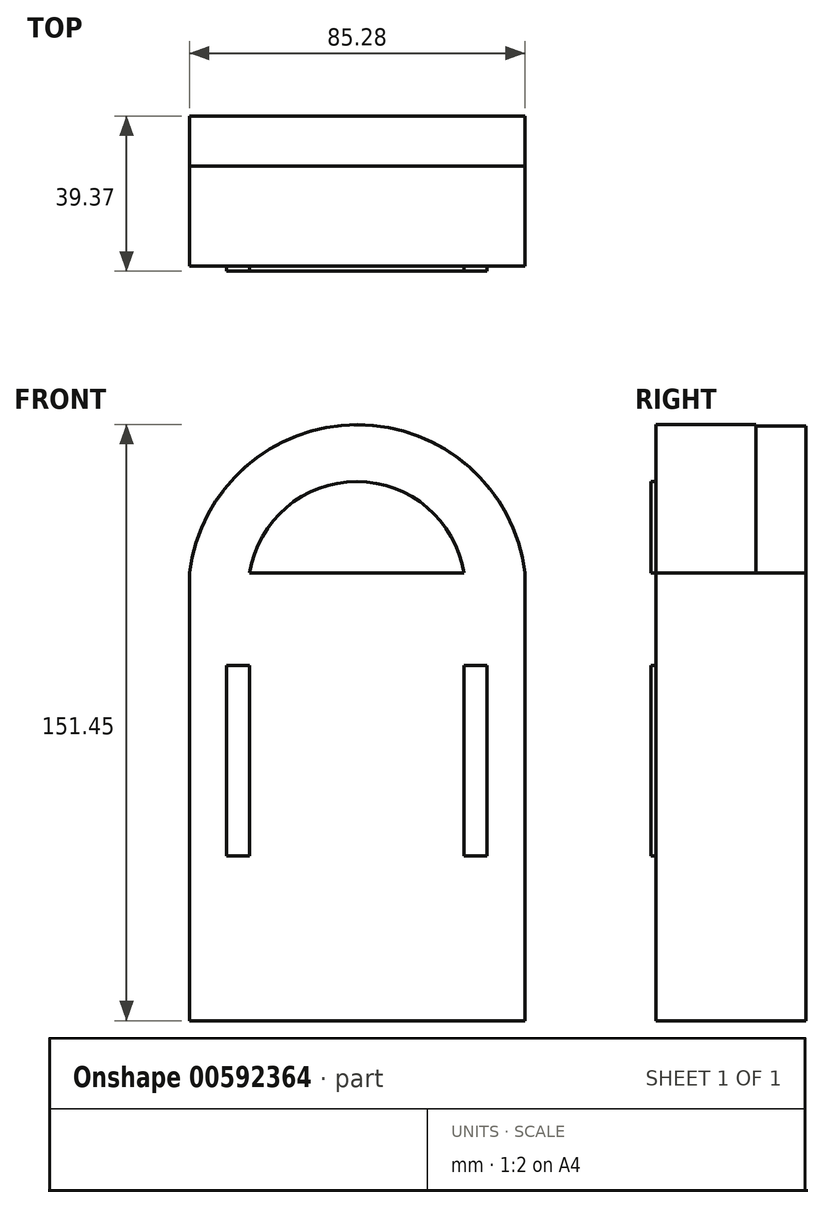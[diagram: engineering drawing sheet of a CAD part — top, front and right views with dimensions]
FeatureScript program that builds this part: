
annotation { "Feature Type Name" : "Feature", "Feature Type Description" : "" }
export const myFeature = defineFeature(function(context is Context, id is Id, definition is map)
    precondition{}
    {
        {
            var Q0;
            Q0=qCreatedBy(makeId("Front.planeOp"),FACE);
            var sketch = newSketch(context, id + "F0", { "sketchPlane" : qUnion([Q0])});
            skLineSegment(sketch, "E0", {"start": v(-42.64, 0) * mm, "end": v(0, 0) * mm});
            skLineSegment(sketch, "E1", {"start": v(0, 0) * mm, "end": v(42.64, 0) * mm});
            skLineSegment(sketch, "E2", {"start": v(-42.64, 0) * mm, "end": v(-42.64, 37.98) * mm});
            skLineSegment(sketch, "E3", {"start": v(42.64, 37.98) * mm, "end": v(42.64, 0) * mm});
            skLineSegment(sketch, "E4", {"start": v(-42.64, 0) * mm, "end": v(-42.64, -75.73) * mm});
            skLineSegment(sketch, "E5", {"start": v(-42.64, -75.73) * mm, "end": v(42.64, -75.73) * mm});
            skLineSegment(sketch, "E6", {"start": v(42.64, -75.73) * mm, "end": v(42.64, 0) * mm});
            skArc(sketch, "E7", {"start": v(42.64, 37.98) * mm, "mid": v(0, 75.72) * mm, "end": v(-42.64, 37.98) * mm});
            skSolve(sketch);
        }
        {
            var Q0;
            Q0=makeQuery(id+"F0.imprint","IMPRINT",FACE,{"disambiguationData":[TD([[makeQuery(id+"F0.imprint","IMPRINT",EDGE,{"derivedFrom":sQuery(id+"F0.wireOp",EDGE,"E0")}),1.0]])]});
            var Q1;
            Q1=makeQuery(id+"F0.imprint","IMPRINT",FACE,{"disambiguationData":[TD([[makeQuery(id+"F0.imprint","IMPRINT",EDGE,{"derivedFrom":sQuery(id+"F0.wireOp",EDGE,"E0")}),-1.0]])]});
            extrude(context, id + "F1", {"entities" : qUnion([Q0, Q1]), "depth" : 25.4 * mm, "offsetDistance" : 25.4 * mm});
        }
        {
            var Q0;
            Q0=makeQuery(id+"F1.opExtrude","CAP_FACE",FACE,{"disambiguationData":[OSD([sQuery(id+"F0.wireOp",EDGE,"E2"),sQuery(id+"F0.wireOp",EDGE,"E3"),sQuery(id+"F0.wireOp",EDGE,"E4"),sQuery(id+"F0.wireOp",EDGE,"E5"),sQuery(id+"F0.wireOp",EDGE,"E6"),sQuery(id+"F0.wireOp",EDGE,"E7")])],"isStart":true});
            var sketch = newSketch(context, id + "F2", { "sketchPlane" : qUnion([Q0])});
            skLineSegment(sketch, "E8", {"start": v(-42.64, 37.98) * mm, "end": v(-42.64, -75.73) * mm});
            skLineSegment(sketch, "E9", {"start": v(-42.64, -75.73) * mm, "end": v(42.64, -75.73) * mm});
            skLineSegment(sketch, "E10", {"start": v(42.64, -75.73) * mm, "end": v(42.64, 37.98) * mm});
            skArc(sketch, "E11", {"start": v(42.64, 37.98) * mm, "mid": v(0, 75.41) * mm, "end": v(-42.64, 37.98) * mm});
            skSolve(sketch);
        }
        {
            var Q0;
            Q0=makeQuery(id+"F2.imprint","IMPRINT",FACE,{"disambiguationData":[TD([[makeQuery(id+"F2.imprint","IMPRINT",EDGE,{"derivedFrom":sQuery(id+"F2.wireOp",EDGE,"E8")}),1.0]])]});
            extrude(context, id + "F3", {"entities" : qUnion([Q0]), "operationType" : NewBodyOperationType.ADD, "depth" : 12.7 * mm, "offsetDistance" : 25.4 * mm});
        }
        {
            var Q0;
            Q0=makeQuery(id+"F1.opExtrude","CAP_FACE",FACE,{"disambiguationData":[OSD([sQuery(id+"F0.wireOp",EDGE,"E2"),sQuery(id+"F0.wireOp",EDGE,"E3"),sQuery(id+"F0.wireOp",EDGE,"E4"),sQuery(id+"F0.wireOp",EDGE,"E5"),sQuery(id+"F0.wireOp",EDGE,"E6"),sQuery(id+"F0.wireOp",EDGE,"E7")])],"isStart":false});
            var sketch = newSketch(context, id + "F4", { "sketchPlane" : qUnion([Q0])});
            skLineSegment(sketch, "E12.bottom", {"start": v(-33.2, 14.46) * mm, "end": v(-27.32, 14.46) * mm});
            skLineSegment(sketch, "E12.top", {"start": v(-33.2, -33.82) * mm, "end": v(-27.32, -33.82) * mm});
            skLineSegment(sketch, "E12.left", {"start": v(-33.2, 14.46) * mm, "end": v(-33.2, -33.82) * mm});
            skLineSegment(sketch, "E12.right", {"start": v(-27.32, 14.46) * mm, "end": v(-27.32, -33.82) * mm});
            skPoint(sketch, "E13.oppositeSnap0", {"position": v(-30.26, 14.46) * mm});
            skLineSegment(sketch, "E13.left", {"start": v(42.64, 14.46) * mm, "end": v(42.64, 14.46) * mm});
            skLineSegment(sketch, "E13.right", {"start": v(32.96, 14.46) * mm, "end": v(32.96, 14.46) * mm});
            skLineSegment(sketch, "E14.bottom", {"start": v(32.96, 14.46) * mm, "end": v(27.08, 14.46) * mm});
            skLineSegment(sketch, "E14.top", {"start": v(32.96, -33.82) * mm, "end": v(27.08, -33.82) * mm});
            skLineSegment(sketch, "E14.left", {"start": v(32.96, 14.46) * mm, "end": v(32.96, -33.82) * mm});
            skLineSegment(sketch, "E14.right", {"start": v(27.08, 14.46) * mm, "end": v(27.08, -33.82) * mm});
            skSolve(sketch);
        }
        {
            var Q0;
            Q0=makeQuery(id+"F4.imprint","IMPRINT",FACE,{"disambiguationData":[TD([[makeQuery(id+"F4.imprint","IMPRINT",EDGE,{"derivedFrom":sQuery(id+"F4.wireOp",EDGE,"E12.bottom")}),-1.0]])]});
            var Q1;
            Q1=makeQuery(id+"F4.imprint","IMPRINT",FACE,{"disambiguationData":[TD([[makeQuery(id+"F4.imprint","IMPRINT",EDGE,{"derivedFrom":sQuery(id+"F4.wireOp",EDGE,"E14.bottom")}),1.0]])]});
            extrude(context, id + "F5", {"entities" : qUnion([Q0, Q1]), "operationType" : NewBodyOperationType.ADD, "depth" : 1.27 * mm, "offsetDistance" : 25.4 * mm});
        }
        {
            var Q0;
            Q0=makeQuery(id+"F1.opExtrude","CAP_FACE",FACE,{"disambiguationData":[OSD([sQuery(id+"F0.wireOp",EDGE,"E2"),sQuery(id+"F0.wireOp",EDGE,"E3"),sQuery(id+"F0.wireOp",EDGE,"E4"),sQuery(id+"F0.wireOp",EDGE,"E5"),sQuery(id+"F0.wireOp",EDGE,"E6"),sQuery(id+"F0.wireOp",EDGE,"E7")])],"isStart":false});
            var sketch = newSketch(context, id + "F6", { "sketchPlane" : qUnion([Q0])});
            skLineSegment(sketch, "E15", {"start": v(-27.32, 37.98) * mm, "end": v(27.08, 37.98) * mm});
            skArc(sketch, "E16", {"start": v(27.08, 37.98) * mm, "mid": v(-0.12, 61.25) * mm, "end": v(-27.32, 37.98) * mm});
            skSolve(sketch);
        }
        {
            var Q0;
            Q0=makeQuery(id+"F6.imprint","IMPRINT",FACE,{"disambiguationData":[TD([[makeQuery(id+"F6.imprint","IMPRINT",EDGE,{"derivedFrom":sQuery(id+"F6.wireOp",EDGE,"E15")}),1.0]])]});
            extrude(context, id + "F7", {"entities" : qUnion([Q0]), "operationType" : NewBodyOperationType.ADD, "depth" : 1.27 * mm, "offsetDistance" : 25.4 * mm});
        }
    });
